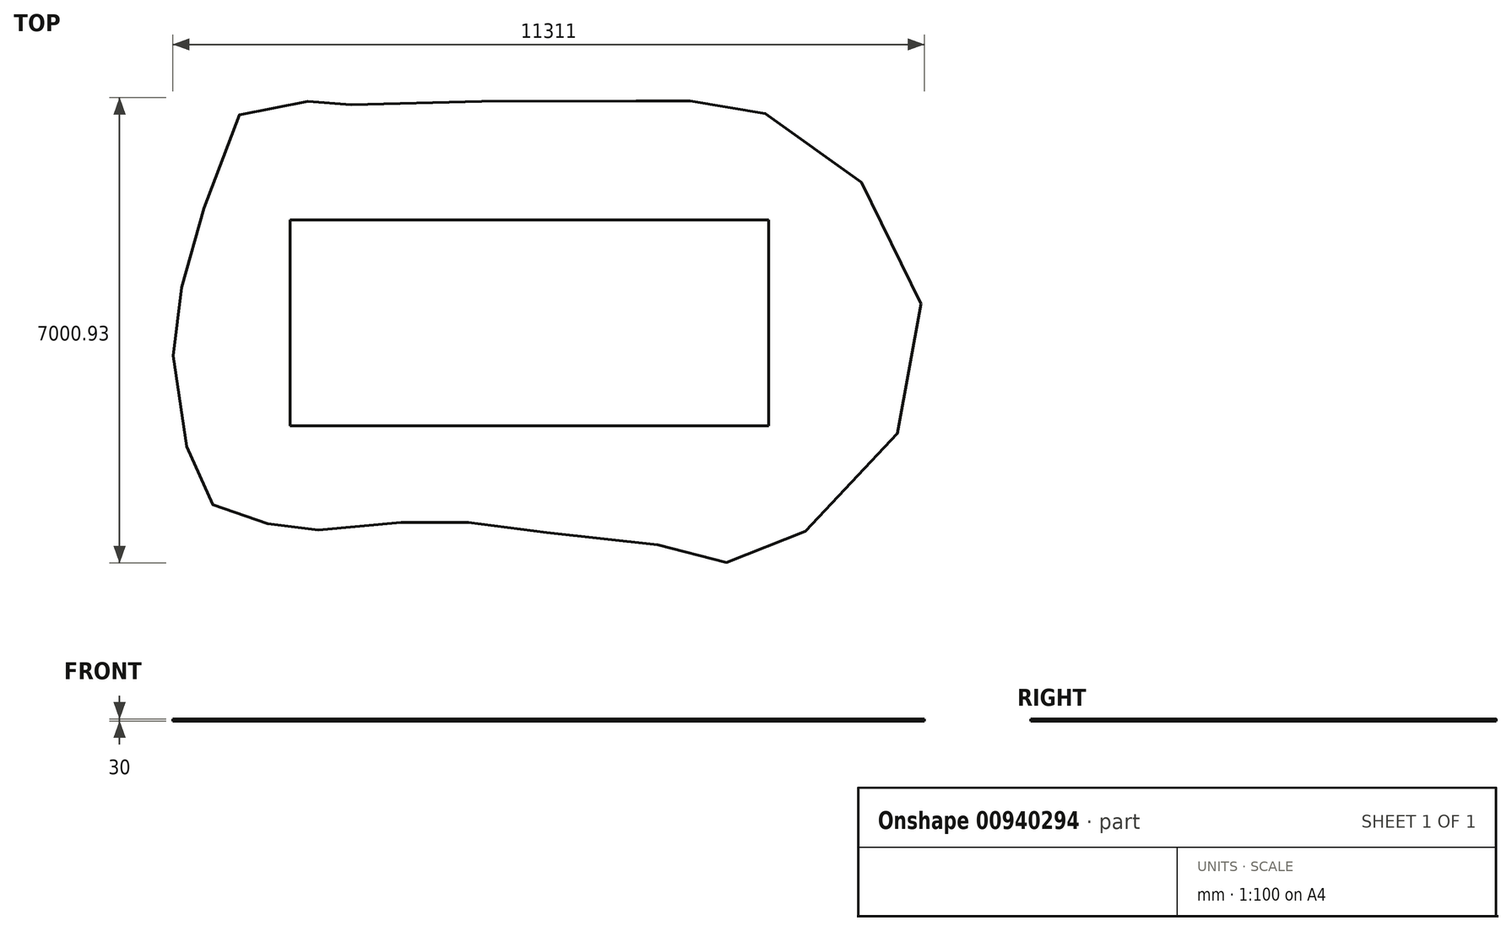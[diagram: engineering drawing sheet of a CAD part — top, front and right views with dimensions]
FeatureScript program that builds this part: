
annotation { "Feature Type Name" : "Feature", "Feature Type Description" : "" }
export const myFeature = defineFeature(function(context is Context, id is Id, definition is map)
    precondition{}
    {
        {
            var Q0;
            Q0=qCreatedBy(makeId("Top.planeOp"),FACE);
            var sketch = newSketch(context, id + "F0", { "sketchPlane" : qUnion([Q0])});
            skLineSegment(sketch, "E0.bottom", {"start": v(-3600, 1550) * mm, "end": v(3600, 1550) * mm});
            skLineSegment(sketch, "E0.top", {"start": v(-3600, -1550) * mm, "end": v(3600, -1550) * mm});
            skLineSegment(sketch, "E0.left", {"start": v(-3600, 1550) * mm, "end": v(-3600, -1550) * mm});
            skLineSegment(sketch, "E0.right", {"start": v(3600, 1550) * mm, "end": v(3600, -1550) * mm});
            skFitSpline(sketch, "E1", {"points": [v(-2679.93, 3286.09) * mm, v(2059.73, 3343.42) * mm, v(2384.63, 3343.42) * mm, v(4123.78, 2884.75) * mm, v(5882.04, -822.9) * mm, v(3301.98, -3574.96) * mm, v(2327.3, -3422.06) * mm, v(-443.88, -3078.06) * mm, v(-1380.35, -2963.39) * mm, v(-3138.61, -3116.28) * mm, v(-3807.52, -3039.83) * mm, v(-4667.54, -2810.5) * mm, v(-5126.21, -1988.7) * mm, v(-5355.55, 0) * mm, v(-5049.77, 1088.26) * mm, v(-4189.75, 3286.09) * mm, v(-3062.17, 3266.98) * mm, v(-2679.93, 3286.09) * mm]});
            skSolve(sketch);
        }
        {
            var Q0;
            Q0 = qSketchRegion(id + "F0", true);
            extrude(context, id + "F1", {"entities" : qUnion([Q0]), "oppositeDirection" : true, "depth" : 30 * mm, "offsetDistance" : 25 * mm});
        }
    });
